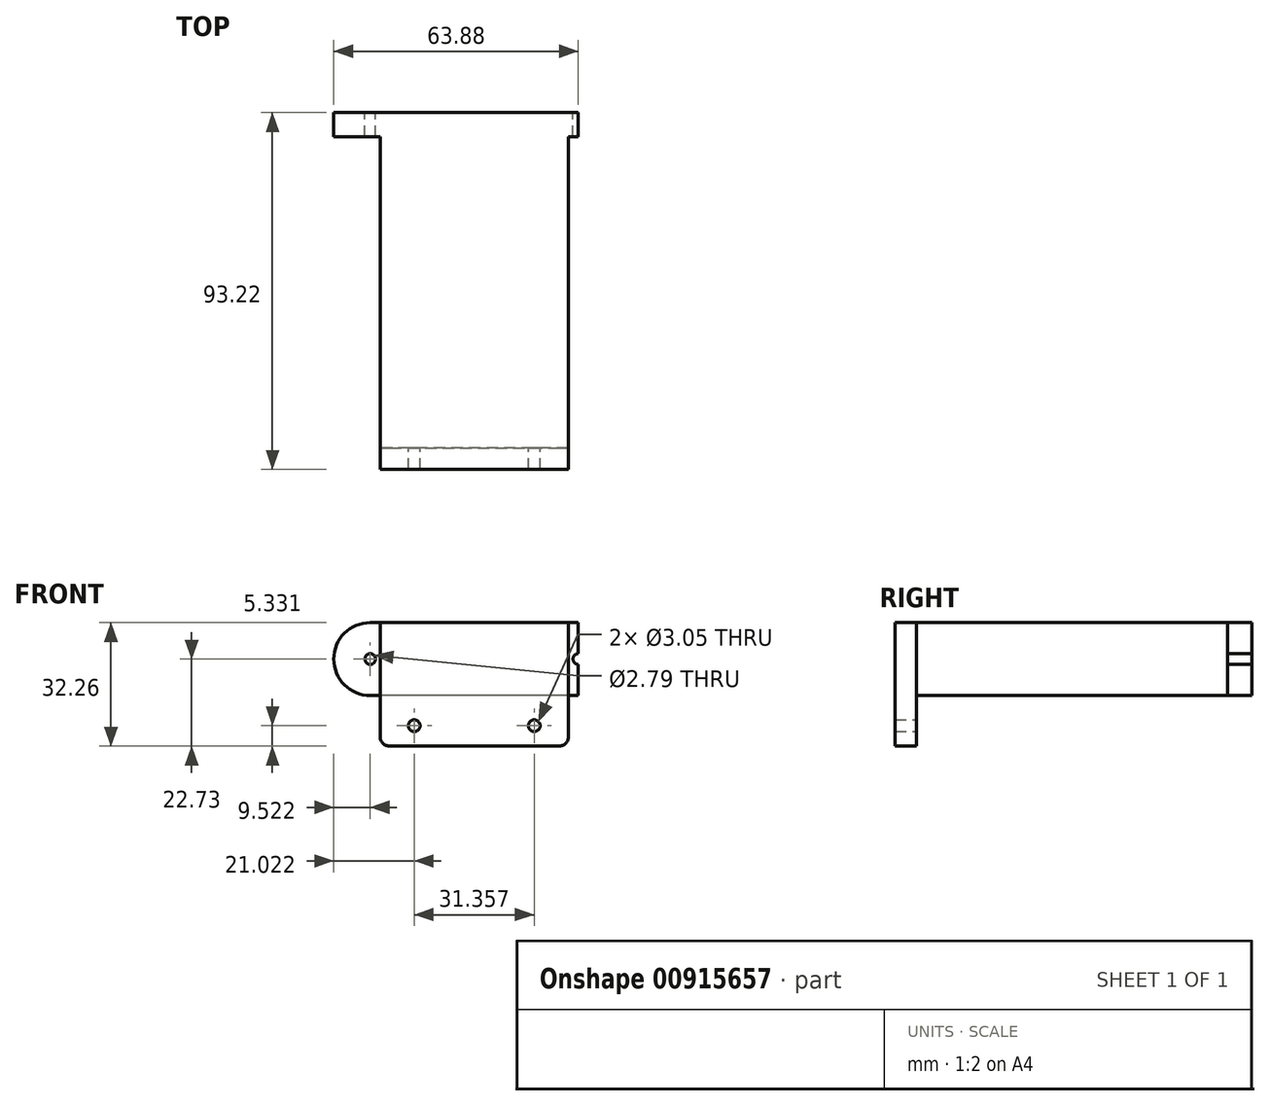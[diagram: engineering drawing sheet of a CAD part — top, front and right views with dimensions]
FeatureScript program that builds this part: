
annotation { "Feature Type Name" : "Feature", "Feature Type Description" : "" }
export const myFeature = defineFeature(function(context is Context, id is Id, definition is map)
    precondition{}
    {
        {
            var Q0;
            Q0=qCreatedBy(makeId("Front.planeOp"),FACE);
            var sketch = newSketch(context, id + "F0", { "sketchPlane" : qUnion([Q0])});
            skLineSegment(sketch, "E0.bottom", {"start": v(27.18, -9.52) * mm, "end": v(-27.18, -9.53) * mm});
            skLineSegment(sketch, "E0.top", {"start": v(27.18, 9.53) * mm, "end": v(-27.18, 9.52) * mm});
            skLineSegment(sketch, "E0.left", {"start": v(27.18, -9.52) * mm, "end": v(27.18, 9.53) * mm});
            skLineSegment(sketch, "E0.right", {"start": v(-27.18, -9.53) * mm, "end": v(-27.18, 9.52) * mm});
            skPoint(sketch, "E0.middle", {"position": v(0, 0) * mm});
            skArc(sketch, "E1", {"start": v(-27.18, 9.52) * mm, "mid": v(-36.7, 0) * mm, "end": v(-27.18, -9.53) * mm});
            skArc(sketch, "E2", {"start": v(27.18, 9.53) * mm, "mid": v(36.7, 0) * mm, "end": v(27.18, -9.52) * mm});
            skCircle(sketch, "E3", {"center": v(-27.18, 0) * mm, "radius": 1.4 * mm});
            skCircle(sketch, "E4.MirrorC", {"center": v(27.18, 0) * mm, "radius": 1.4 * mm});
            skSolve(sketch);
        }
        {
            var Q0;
            {var subQ0=sQuery(id+"F0.wireOp",EDGE,"E1");Q0=makeQuery(id+"F0.imprint","IMPRINT",FACE,{"disambiguationData":[TD([[makeQuery(id+"F0.imprint","IMPRINT",EDGE,{"derivedFrom":subQ0}),1.0]])]});}
            var Q1;
            {var subQ5=sQuery(id+"F0.wireOp",EDGE,"E0.bottom");Q1=makeQuery(id+"F0.imprint","IMPRINT",FACE,{"disambiguationData":[TD([[makeQuery(id+"F0.imprint","IMPRINT",EDGE,{"derivedFrom":subQ5}),-1.0]])]});}
            var Q2;
            {var subQ0=sQuery(id+"F0.wireOp",EDGE,"E2");Q2=makeQuery(id+"F0.imprint","IMPRINT",FACE,{"disambiguationData":[TD([[makeQuery(id+"F0.imprint","IMPRINT",EDGE,{"derivedFrom":subQ0}),-1.0]])]});}
            extrude(context, id + "F1", {"entities" : qUnion([Q0, Q1, Q2]), "depth" : 6.35 * mm, "offsetDistance" : 25.4 * mm});
        }
        {
            var Q0;
            Q0=makeQuery(id+"F1.opExtrude","CAP_FACE",FACE,{"disambiguationData":[OSD([sQuery(id+"F0.wireOp",EDGE,"E0.bottom"),sQuery(id+"F0.wireOp",EDGE,"E0.top"),sQuery(id+"F0.wireOp",EDGE,"E1"),sQuery(id+"F0.wireOp",EDGE,"E2"),sQuery(id+"F0.wireOp",EDGE,"E3"),sQuery(id+"F0.wireOp",EDGE,"E4.MirrorC")])],"isStart":false});
            var sketch = newSketch(context, id + "F2", { "sketchPlane" : qUnion([Q0])});
            skLineSegment(sketch, "E5.bottom", {"start": v(24.6, -9.52) * mm, "end": v(-24.6, -9.52) * mm});
            skLineSegment(sketch, "E5.top", {"start": v(24.6, 9.52) * mm, "end": v(-24.6, 9.52) * mm});
            skLineSegment(sketch, "E5.left", {"start": v(24.6, -9.52) * mm, "end": v(24.6, 9.52) * mm});
            skLineSegment(sketch, "E5.right", {"start": v(-24.6, -9.52) * mm, "end": v(-24.6, 9.52) * mm});
            skPoint(sketch, "E5.middle", {"position": v(0, 0) * mm});
            skSolve(sketch);
        }
        {
            var Q0;
            Q0 = qSketchRegion(id + "F2", true);
            extrude(context, id + "F3", {"entities" : qUnion([Q0]), "operationType" : NewBodyOperationType.ADD, "depth" : 81.28 * mm, "offsetDistance" : 25.4 * mm});
        }
        {
            var Q0;
            Q0=makeQuery(id+"F3.opExtrude","CAP_FACE",FACE,{"disambiguationData":[OSD([sQuery(id+"F2.wireOp",EDGE,"E5.bottom"),sQuery(id+"F2.wireOp",EDGE,"E5.top"),sQuery(id+"F2.wireOp",EDGE,"E5.left"),sQuery(id+"F2.wireOp",EDGE,"E5.right")])],"isStart":false});
            var sketch = newSketch(context, id + "F4", { "sketchPlane" : qUnion([Q0])});
            skLineSegment(sketch, "E6.bottom", {"start": v(-24.6, 9.52) * mm, "end": v(24.65, 9.52) * mm});
            skLineSegment(sketch, "E6.top", {"start": v(-24.6, -22.73) * mm, "end": v(24.65, -22.73) * mm});
            skLineSegment(sketch, "E6.left", {"start": v(-24.6, 9.52) * mm, "end": v(-24.6, -22.73) * mm});
            skLineSegment(sketch, "E6.right", {"start": v(24.65, 9.52) * mm, "end": v(24.65, -22.73) * mm});
            skPoint(sketch, "E7", {"position": v(-15.68, -17.4) * mm});
            skPoint(sketch, "E8.MirrorP", {"position": v(15.68, -17.4) * mm});
            skCircle(sketch, "E9", {"center": v(-15.68, -17.4) * mm, "radius": 1.52 * mm});
            skCircle(sketch, "E10.MirrorC", {"center": v(15.68, -17.4) * mm, "radius": 1.52 * mm});
            skSolve(sketch);
        }
        {
            var Q0;
            {var subQ4=makeQuery(id+"F3.opExtrude","CAP_EDGE",EDGE,{"disambiguationData":[OSD([sQuery(id+"F2.wireOp",EDGE,"E5.bottom")])],"isStart":false});Q0=makeQuery(id+"F4.imprint","IMPRINT",FACE,{"disambiguationData":[TD([[makeQuery(id+"F4.imprint","IMPRINT",EDGE,{"derivedFrom":subQ4}),-1.0]])]});}
            var Q1;
            {var subQ3=sQuery(id+"F4.wireOp",EDGE,"E6.top");Q1=makeQuery(id+"F4.imprint","IMPRINT",FACE,{"disambiguationData":[TD([[makeQuery(id+"F4.imprint","IMPRINT",EDGE,{"derivedFrom":subQ3}),1.0]])]});}
            extrude(context, id + "F5", {"entities" : qUnion([Q0, Q1]), "operationType" : NewBodyOperationType.ADD, "depth" : 5.6 * mm, "offsetDistance" : 25.4 * mm});
        }
        {
            var Q0;
            Q0=makeQuery(id+"F5.opExtrude","SWEPT_EDGE",EDGE,{"disambiguationData":[OSD([sQuery(id+"F4.wireOp",EDGE,"E6.top"),sQuery(id+"F4.wireOp",EDGE,"E6.left")])]});
            var Q1;
            Q1=makeQuery(id+"F5.opExtrude","SWEPT_EDGE",EDGE,{"disambiguationData":[OSD([sQuery(id+"F4.wireOp",EDGE,"E6.top"),sQuery(id+"F4.wireOp",EDGE,"E6.right")])]});
            fillet(context, id + "F6", {"entities" : qUnion([Q0, Q1]), "radius" : 2.54 * mm, "tangentPropagation" : true, "allowEdgeOverflow" : false});
        }
    });
